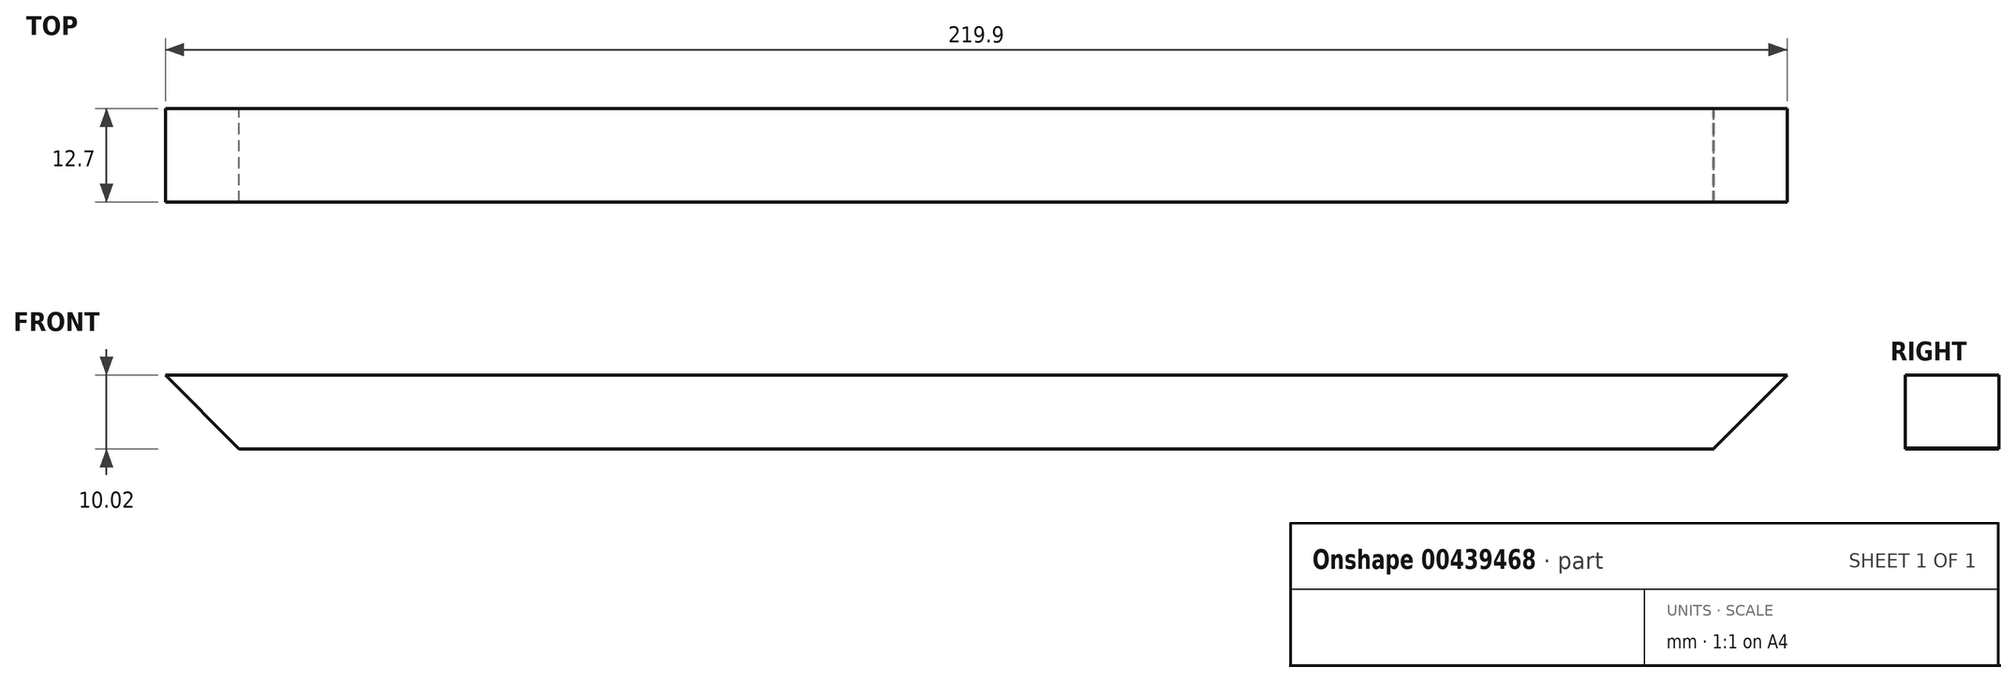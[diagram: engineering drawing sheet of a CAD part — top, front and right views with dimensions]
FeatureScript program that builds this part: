
annotation { "Feature Type Name" : "Feature", "Feature Type Description" : "" }
export const myFeature = defineFeature(function(context is Context, id is Id, definition is map)
    precondition{}
    {
        {
            var Q0;
            Q0=qCreatedBy(makeId("Front.planeOp"),FACE);
            var sketch = newSketch(context, id + "F0", { "sketchPlane" : qUnion([Q0])});
            skLineSegment(sketch, "E0.bottom", {"start": v(100, 5) * mm, "end": v(-100, 5) * mm});
            skLineSegment(sketch, "E0.top", {"start": v(100, -5) * mm, "end": v(-100, -5) * mm});
            skLineSegment(sketch, "E0.left", {"start": v(100, 5) * mm, "end": v(100, -5) * mm});
            skLineSegment(sketch, "E0.right", {"start": v(-100, 5) * mm, "end": v(-100, -5) * mm});
            skPoint(sketch, "E0.middle", {"position": v(0, 0) * mm});
            skSolve(sketch);
        }
        {
            var Q0;
            Q0 = qSketchRegion(id + "F0", true);
            extrude(context, id + "F1", {"entities" : qUnion([Q0]), "depth" : 12.7 * mm});
        }
        {
            var Q0;
            Q0=qCreatedBy(makeId("Front.planeOp"),FACE);
            var sketch = newSketch(context, id + "F2", { "sketchPlane" : qUnion([Q0])});
            skLineSegment(sketch, "E1", {"start": v(99.9, 5) * mm, "end": v(109.9, 5) * mm});
            skLineSegment(sketch, "E2", {"start": v(109.9, 5) * mm, "end": v(99.9, -5) * mm});
            skLineSegment(sketch, "E3", {"start": v(99.9, -5) * mm, "end": v(99.9, 5) * mm});
            skSolve(sketch);
        }
        {
            var Q0;
            Q0 = qSketchRegion(id + "F2", true);
            extrude(context, id + "F3", {"entities" : qUnion([Q0]), "operationType" : NewBodyOperationType.ADD, "depth" : 12.7 * mm});
        }
        {
            var Q0;
            Q0=qCreatedBy(makeId("Front.planeOp"),FACE);
            var sketch = newSketch(context, id + "F4", { "sketchPlane" : qUnion([Q0])});
            skLineSegment(sketch, "E4", {"start": v(-100, -5) * mm, "end": v(-100, 5.01) * mm});
            skLineSegment(sketch, "E5", {"start": v(-100, 5.01) * mm, "end": v(-110, 5.01) * mm});
            skLineSegment(sketch, "E6", {"start": v(-110, 5.01) * mm, "end": v(-100, -5) * mm});
            skSolve(sketch);
        }
        {
            var Q0;
            Q0 = qSketchRegion(id + "F4", true);
            extrude(context, id + "F5", {"entities" : qUnion([Q0]), "operationType" : NewBodyOperationType.ADD, "depth" : 12.7 * mm});
        }
    });
